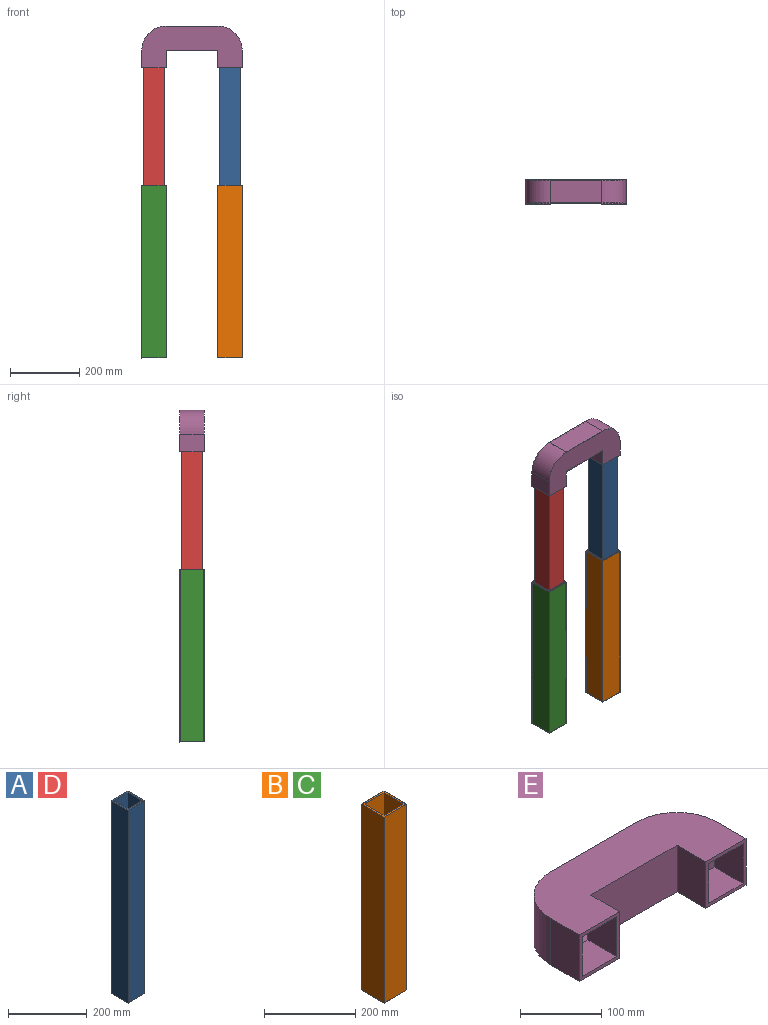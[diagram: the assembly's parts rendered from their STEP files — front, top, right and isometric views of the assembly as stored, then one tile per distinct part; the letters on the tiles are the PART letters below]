
ASSEMBLY  parts=5 mates=4
PART A: 20 faces, bbox 60x60x600 mm
  f0: plane 60x60mm, normal (0,0,-1), area 236mm2, adj f5,f6,f7,f8,f14,f15,f16,f17
  f1: plane 52x52mm, normal (0,0,-1), area 204mm2, adj f2,f3,f4,f9,f11,f12,f13,f18
  f2: plane 600x50mm, normal (0,-1,0), area 30000mm2, adj f1,f3,f9,f10
  f3: plane 600x50mm, normal (-1,0,0), area 30000mm2, adj f1,f2,f4,f10
  f4: plane 600x50mm, normal (0,1,0), area 30000mm2, adj f1,f3,f9,f10
  f5: plane 600x60mm, normal (-1,0,0), area 36000mm2, adj f0,f6,f8,f10
  f6: plane 600x60mm, normal (0,-1,0), area 36000mm2, adj f0,f5,f7,f10
  f7: plane 600x60mm, normal (1,0,0), area 36000mm2, adj f0,f6,f8,f10
  f8: plane 600x60mm, normal (0,1,0), area 36000mm2, adj f0,f5,f7,f10
  f9: plane 600x50mm, normal (1,0,0), area 30000mm2, adj f1,f2,f4,f10
  f10: plane 60x60mm, normal (0,0,1), area 1100mm2, adj f2,f3,f4,f5,f6,f7,f8,f9
  f11: plane 599x52mm, normal (0,1,0), area 31148mm2, adj f1,f12,f18,f19
  f12: plane 599x52mm, normal (1,0,0), area 31148mm2, adj f1,f11,f13,f19
  f13: plane 599x52mm, normal (0,-1,0), area 31148mm2, adj f1,f12,f18,f19
  f14: plane 599x58mm, normal (1,0,0), area 34742mm2, adj f0,f15,f17,f19
  f15: plane 599x58mm, normal (0,1,0), area 34742mm2, adj f0,f14,f16,f19
  f16: plane 599x58mm, normal (-1,0,0), area 34742mm2, adj f0,f15,f17,f19
  f17: plane 599x58mm, normal (0,-1,0), area 34742mm2, adj f0,f14,f16,f19
  f18: plane 599x52mm, normal (-1,0,0), area 31148mm2, adj f1,f11,f13,f19
  f19: plane 58x58mm, normal (0,0,-1), area 660mm2, adj f11,f12,f13,f14,f15,f16,f17,f18
PART B: 20 faces, bbox 70x70x500 mm
  f0: plane 70x70mm, normal (0,0,-1), area 276mm2, adj f5,f6,f7,f8,f14,f15,f16,f17
  f1: plane 62x62mm, normal (0,0,-1), area 244mm2, adj f2,f3,f4,f9,f11,f12,f13,f18
  f2: plane 500x60mm, normal (0,1,0), area 30000mm2, adj f1,f3,f9,f10
  f3: plane 500x60mm, normal (1,0,0), area 30000mm2, adj f1,f2,f4,f10
  f4: plane 500x60mm, normal (0,-1,0), area 30000mm2, adj f1,f3,f9,f10
  f5: plane 500x70mm, normal (-1,0,0), area 35000mm2, adj f0,f6,f8,f10
  f6: plane 500x70mm, normal (0,-1,0), area 35000mm2, adj f0,f5,f7,f10
  f7: plane 500x70mm, normal (1,0,0), area 35000mm2, adj f0,f6,f8,f10
  f8: plane 500x70mm, normal (0,1,0), area 35000mm2, adj f0,f5,f7,f10
  f9: plane 500x60mm, normal (-1,0,0), area 30000mm2, adj f1,f2,f4,f10
  f10: plane 70x70mm, normal (0,0,1), area 1300mm2, adj f2,f3,f4,f5,f6,f7,f8,f9
  f11: plane 499x62mm, normal (0,-1,0), area 30938mm2, adj f1,f12,f18,f19
  f12: plane 499x62mm, normal (-1,0,0), area 30938mm2, adj f1,f11,f13,f19
  f13: plane 499x62mm, normal (0,1,0), area 30938mm2, adj f1,f12,f18,f19
  f14: plane 499x68mm, normal (1,0,0), area 33932mm2, adj f0,f15,f17,f19
  f15: plane 499x68mm, normal (0,1,0), area 33932mm2, adj f0,f14,f16,f19
  f16: plane 499x68mm, normal (-1,0,0), area 33932mm2, adj f0,f15,f17,f19
  f17: plane 499x68mm, normal (0,-1,0), area 33932mm2, adj f0,f14,f16,f19
  f18: plane 499x62mm, normal (1,0,0), area 30938mm2, adj f1,f11,f13,f19
  f19: plane 68x68mm, normal (0,0,-1), area 780mm2, adj f11,f12,f13,f14,f15,f16,f17,f18
PART C: same geometry as B
PART D: same geometry as A
PART E: 29 faces, bbox 290x120x70 mm
  f0: plane 70x70mm, normal (0,-1,0), area 1300mm2, adj f3,f5,f8,f9,f17,f18,f19,f20
  f1: plane 70x70mm, normal (0,-1,0), area 1300mm2, adj f3,f5,f10,f11,f12,f13,f14,f15
  f2: plane 150x70mm, normal (0,-1,0), area 10500mm2, adj f3,f5,f9,f10
  f3: plane 290x120mm, normal (0,0,1), area 25196.9mm2, adj f0,f1,f2,f4,f6,f7,f8,f9
  f4: cylinder r=70mm len=70mm, axis (0,0,1), area 7696.9mm2, adj f3,f5,f6,f11
  f5: plane 290x120mm, normal (0,0,-1), area 25196.9mm2, adj f0,f1,f2,f4,f6,f7,f8,f9
  f6: plane 150x70mm, normal (0,1,0), area 10500mm2, adj f3,f4,f5,f7
  f7: cylinder r=70mm len=70mm, axis (0,0,1), area 7696.9mm2, adj f3,f5,f6,f8
  f8: plane 70x50mm, normal (-1,0,0), area 3500mm2, adj f0,f3,f5,f7
  f9: plane 70x50mm, normal (1,0,0), area 3500mm2, adj f0,f2,f3,f5
  f10: plane 70x50mm, normal (-1,0,0), area 3500mm2, adj f1,f2,f3,f5
  f11: plane 70x50mm, normal (1,0,0), area 3500mm2, adj f1,f3,f4,f5
  f12: plane 60x50mm, normal (1,0,0), area 3000mm2, adj f1,f13,f15,f16
  f13: plane 60x50mm, normal (0,0,1), area 3000mm2, adj f1,f12,f14,f16
  f14: plane 60x50mm, normal (-1,0,0), area 3000mm2, adj f1,f13,f15,f16
  f15: plane 60x50mm, normal (0,0,-1), area 3000mm2, adj f1,f12,f14,f16
  f16: plane 60x60mm, normal (0,-1,0), area 3600mm2, adj f12,f13,f14,f15
  f17: plane 60x50mm, normal (0,0,-1), area 3000mm2, adj f0,f18,f20,f21
  f18: plane 60x50mm, normal (1,0,0), area 3000mm2, adj f0,f17,f19,f21
  f19: plane 60x50mm, normal (0,0,1), area 3000mm2, adj f0,f18,f20,f21
  f20: plane 60x50mm, normal (-1,0,0), area 3000mm2, adj f0,f17,f19,f21
  f21: plane 65x65mm, normal (0,1,0), area 625mm2, adj f17,f18,f19,f20,f22,f24,f27,f28
  f22: plane 284.95x67.5mm, normal (0,0,1), area 16732mm2, adj f21,f23,f25,f26,f27,f28
  f23: cylinder r=67.5mm len=67.45mm, axis (0,0,1), area 6729.3mm2, adj f22,f24,f25,f26
  f24: plane 284.95x67.5mm, normal (0,0,-1), area 16732mm2, adj f21,f23,f25,f26,f27,f28
  f25: plane 219.95x65mm, normal (0,1,0), area 14297mm2, adj f22,f23,f24,f28
  f26: plane 150x65mm, normal (0,-1,0), area 9750mm2, adj f22,f23,f24,f27
  f27: cylinder r=67.5mm len=67.5mm, axis (0,0,1), area 6891.9mm2, adj f21,f22,f24,f26
  f28: plane 65x2.5mm, normal (-1,0,0), area 162.5mm2, adj f21,f22,f24,f25
PLACE A t=(-105.67,-1397.38,1401.61)mm
PLACE B t=(-105.67,-1397.38,1111.61)mm fixed
PLACE C t=(-325.67,-1397.38,1111.61)mm fixed
PLACE D t=(-325.67,-1397.38,1401.61)mm
PLACE E rot(axis=(1,0,0),90deg) t=(-165.67,-1369.73,1951.61)mm
MATE slider B.f1 <-> A.f1  axis (0,0,-1) through (-135.67,-1399.73,1111.61)mm
MATE fastened E.f20 <-> D.f7  axis (-1,0,0) through (-325.67,-1369.73,2001.61)mm
MATE slider C.f1 <-> D.f1  axis (0,0,-1) through (-355.67,-1399.73,1111.61)mm
MATE fastened A.f10 <-> E.f16  axis (0,0,1) through (-135.67,-1399.73,2001.61)mm
